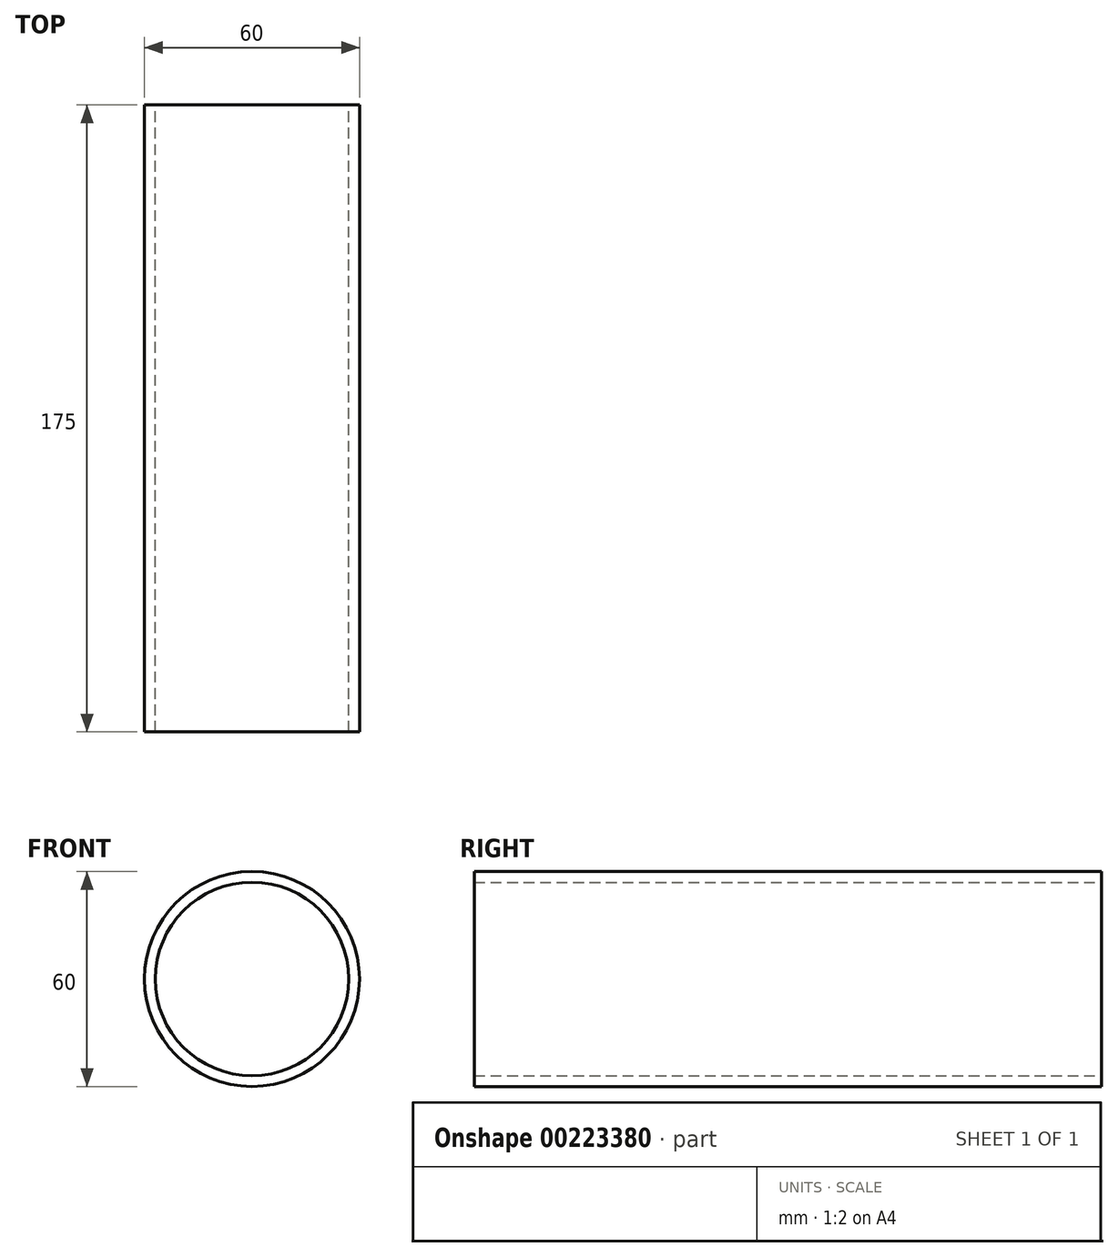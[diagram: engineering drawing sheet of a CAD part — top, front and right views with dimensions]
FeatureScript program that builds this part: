
annotation { "Feature Type Name" : "Feature", "Feature Type Description" : "" }
export const myFeature = defineFeature(function(context is Context, id is Id, definition is map)
    precondition{}
    {
        {
            var Q0;
            Q0=qCreatedBy(makeId("Front.planeOp"),FACE);
            var sketch = newSketch(context, id + "F0", { "sketchPlane" : qUnion([Q0])});
            skCircle(sketch, "E0", {"center": v(0, 0) * mm, "radius": 27 * mm});
            skCircle(sketch, "E1", {"center": v(0, 0) * mm, "radius": 30 * mm});
            skSolve(sketch);
        }
        {
            var Q0;
            Q0 = qSketchRegion(id + "F0", true);
            extrude(context, id + "F1", {"entities" : qUnion([Q0]), "depth" : 25 * mm});
        }
        {
            var Q0;
            Q0 = qSketchRegion(id + "F0", true);
            extrude(context, id + "F2", {"entities" : qUnion([Q0]), "operationType" : NewBodyOperationType.ADD, "depth" : 175 * mm});
        }
    });
